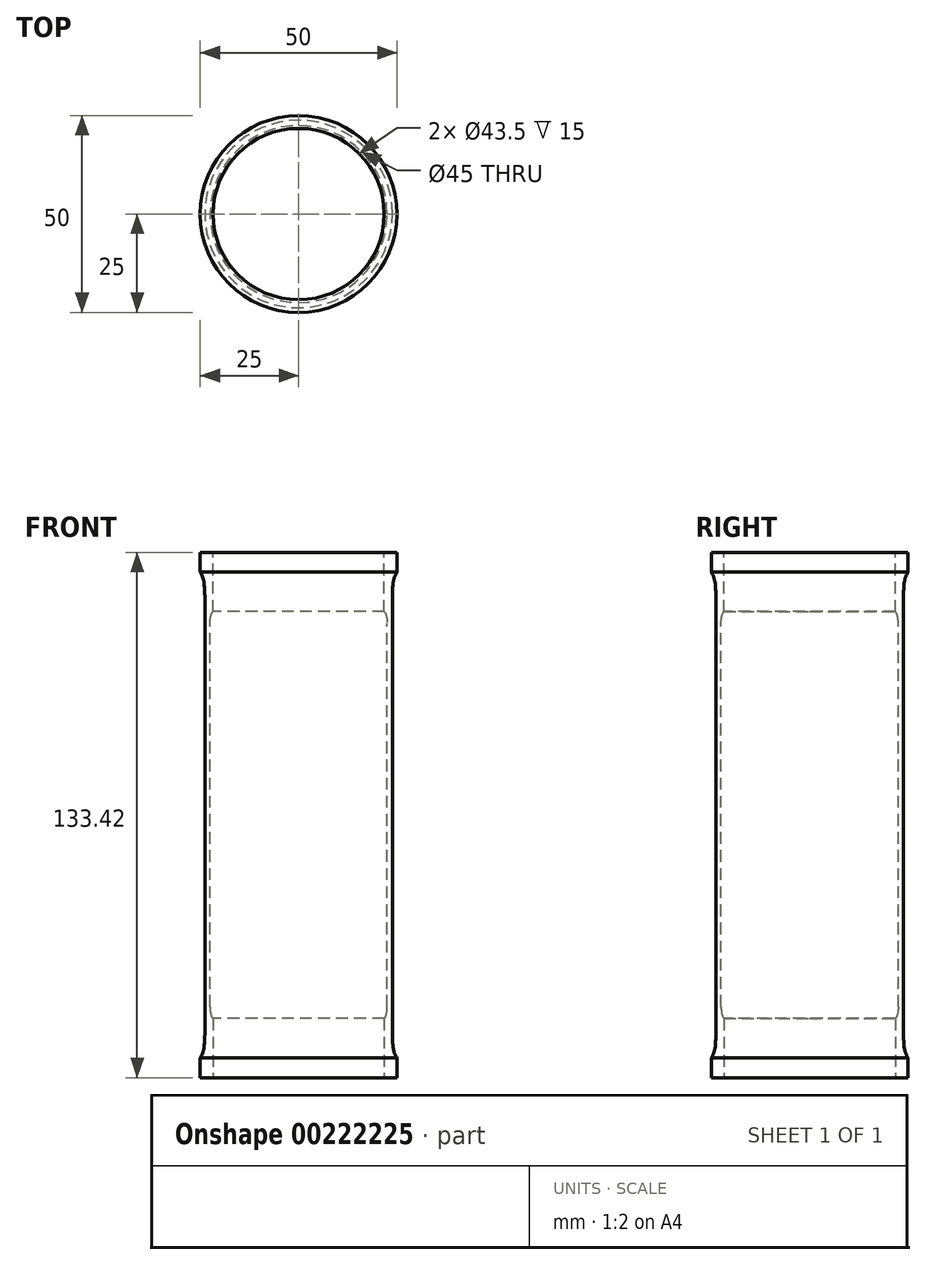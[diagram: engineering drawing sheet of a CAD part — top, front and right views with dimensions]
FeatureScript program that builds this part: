
annotation { "Feature Type Name" : "Feature", "Feature Type Description" : "" }
export const myFeature = defineFeature(function(context is Context, id is Id, definition is map)
    precondition{}
    {
        {
            var Q0;
            Q0=qCreatedBy(makeId("Front.planeOp"),FACE);
            var sketch = newSketch(context, id + "F0", { "sketchPlane" : qUnion([Q0])});
            skLineSegment(sketch, "E0.bottom", {"start": v(21.75, 66.7) * mm, "end": v(21.75, 51.7) * mm});
            skLineSegment(sketch, "E0.top", {"start": v(25, 66.7) * mm, "end": v(25, 61.7) * mm});
            skLineSegment(sketch, "E0.left", {"start": v(21.75, 66.7) * mm, "end": v(25, 66.7) * mm});
            skLineSegment(sketch, "E1", {"start": v(0, 66.7) * mm, "end": v(0, 0) * mm});
            skLineSegment(sketch, "E2", {"start": v(22.5, 48.7) * mm, "end": v(22.5, 0) * mm});
            skFitSpline(sketch, "E3", {"points": [v(21.75, 51.7) * mm, v(22.5, 48.7) * mm], "startDerivative": vector(1.82, -1.9) * mm, "endDerivative": vector(0, -3.45) * mm});
            skLineSegment(sketch, "E4", {"start": v(23.8, 51.7) * mm, "end": v(23.8, 0) * mm});
            skLineSegment(sketch, "E5", {"start": v(23.8, 0) * mm, "end": v(0, 0) * mm});
            skPoint(sketch, "E5.endSnap0", {"position": v(0, 0) * mm});
            skFitSpline(sketch, "E6", {"points": [v(25, 61.7) * mm, v(23.8, 51.7) * mm], "startDerivative": vector(-3.48, -5.4) * mm, "endDerivative": vector(0, -19.94) * mm});
            skSolve(sketch);
        }
        {
            var Q0;
            Q0=makeQuery(id+"F0.imprint","IMPRINT",FACE,{"disambiguationData":[TD([[makeQuery(id+"F0.imprint","IMPRINT",EDGE,{"derivedFrom":sQuery(id+"F0.wireOp",EDGE,"E0.bottom")}),1.0]])]});
            var Q1;
            Q1=sQuery(id+"F0.wireOp",EDGE,"E1");
            revolve(context, id + "F1", {"entities" : qUnion([Q0]), "axis" : qUnion([Q1]), "revolveType" : RevolveType.FULL});
        }
        {
            var Q0;
            Q0=makeQuery(id+"F1.opRevolve","SWEPT_BODY",BODY,{"disambiguationData":[OSD([sQuery(id+"F0.wireOp",EDGE,"E0.bottom"),sQuery(id+"F0.wireOp",EDGE,"E0.top"),sQuery(id+"F0.wireOp",EDGE,"E0.left"),sQuery(id+"F0.wireOp",EDGE,"E2"),sQuery(id+"F0.wireOp",EDGE,"E3"),sQuery(id+"F0.wireOp",EDGE,"E4"),sQuery(id+"F0.wireOp",EDGE,"E5"),sQuery(id+"F0.wireOp",EDGE,"E6")])]});
            var Q1;
            Q1=makeQuery(id+"F1.opRevolve","SWEPT_FACE",FACE,{"disambiguationData":[OSD([sQuery(id+"F0.wireOp",EDGE,"E5")])]});
            mirror(context, id + "F2", {"operationType" : NewBodyOperationType.ADD, "entities" : qUnion([Q0]), "mirrorPlane" : qUnion([Q1])});
        }
    });
